# Revit family: Deca_Acabamento para caixa de descarga embutida_H Quadra Duo_4900.HQD.DUO
name_source: partatom
category: Plumbing Fixtures
units: mm (PartAtom-declared; Revit-internal decimal feet)

## family parameters
Cut with Voids When Loaded = No
Host = Face
Part Type = Normal
Room Calculation Point = No
Round Connector Dimension = Use Diameter
Shared = No

## types (3) — shared parameters
Acompanha o Produto = -
Aprovado por = quattroD
Atendimento ao Cliente = 0800-0117073
Categoria = SISTEMAS DE DESCARGA
Composição Anel Vedação = -
Composição Assento = -
Composição Básica = Plástico de Engenharia
Composição Componente = -
Consumo = -
Cor Interna = -
Cor Secundária = -
Cores Componente = -
Criado por = quattroD
Código Pai = 4900.HQD.DUO
Default Elevation = 1100 mm
Description = Acabamento para caixa de descarga embutida
Informações Complementares = -
Itens de Instalação = 2500.CX.PN.AF; 2501.CX.PN.AF; 2502.CX.PN.AF
Linha = Acabamento p/ Caixa embut
Manufacturer = Deca
Norma = Não Possui
Pressão máx. funcionamento = -
Pressão mín. Aquec. Acúmulo = -
Pressão mín. Aquec. Passagem = -
Pressão mín. funcionamento = -
Saída de Esgoto = -
Segmento = Válvula Hydra
Tipo de dispositivo economizador = -
Tipo de mecanismo utilizado = -
Tipo de rosca de entrada = -
Tipo de rosca de saída = -
URL = www.deca.com.br
Vazão na Pressão máx. (L/min) = -
Vazão na Pressão mín. (L/min) = -

## per-type parameters (varying)
| type | Cor Principal | Material | Model | Peso Líquido (Kg) |
| 4900.E.HQD.DUO.BR_Branco | Branco | Deca_Branco | 4900.E.HQD.DUO.BR | 4 |
| 4900.F.HQD.DUO.PT_Preto Fosco | Preto fosco | Deca_Preto | 4900.F.HQD.DUO.PT | 0.383 |
| 4900.C.HQD.DUO_Cromado | Cromado | Deca_Cromado | 4900.C.HQD.DUO | 4 |

## geometry (parser evidence)
native form markers: Sweep x3
no freeform markers — native parametric forms only
